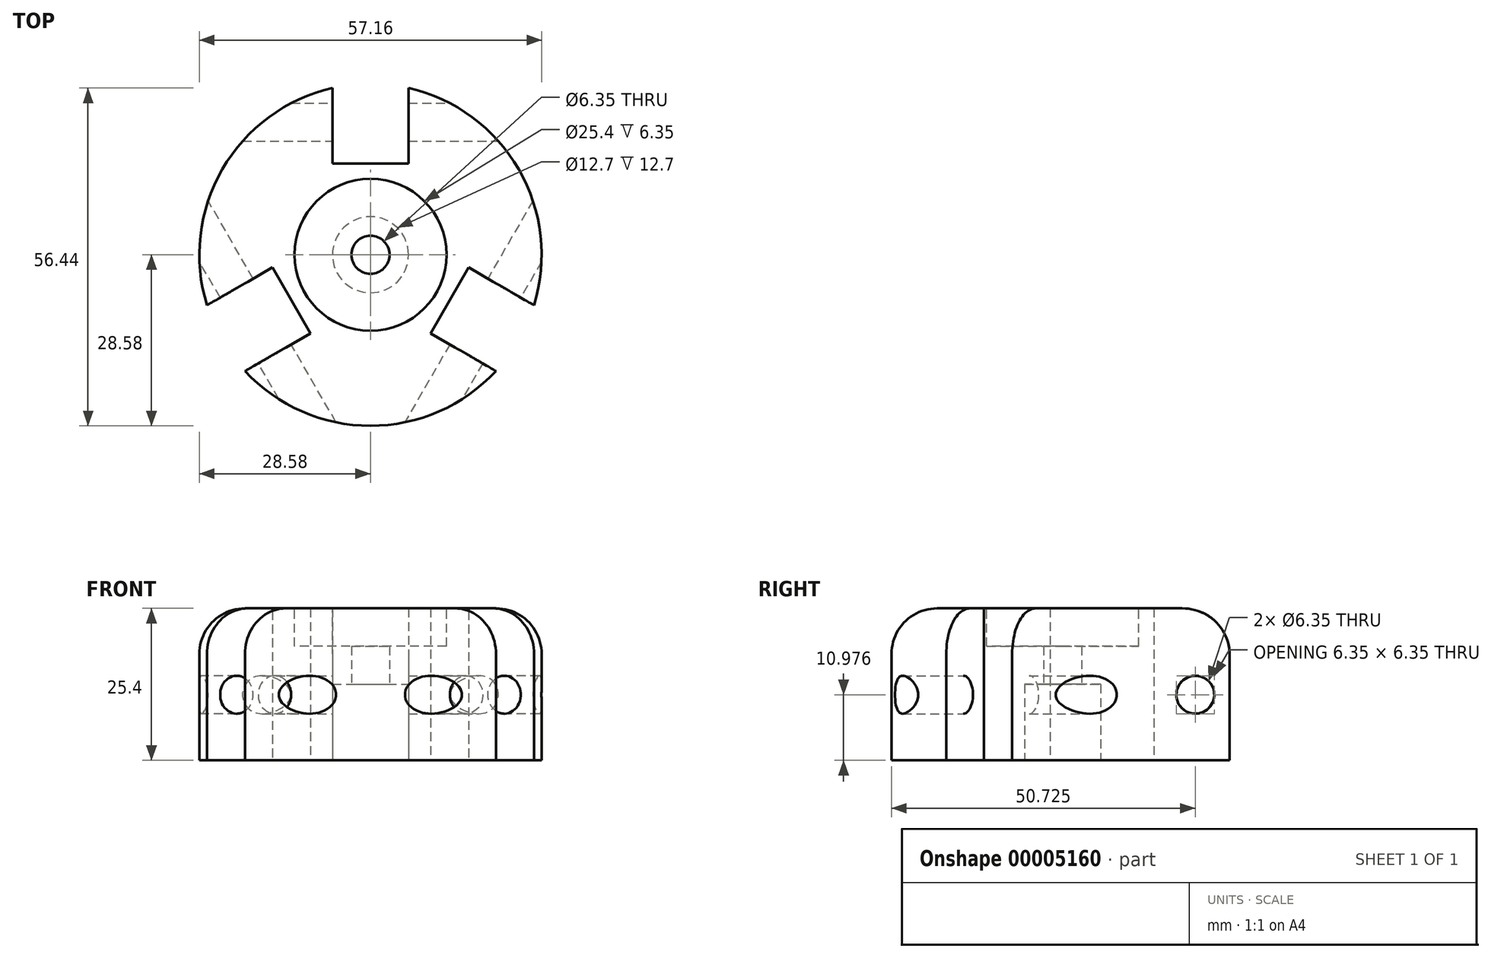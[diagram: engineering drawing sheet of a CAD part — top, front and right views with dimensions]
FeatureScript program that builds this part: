
annotation { "Feature Type Name" : "Feature", "Feature Type Description" : "" }
export const myFeature = defineFeature(function(context is Context, id is Id, definition is map)
    precondition{}
    {
        {
            var Q0;
            Q0=qCreatedBy(makeId("Top.planeOp"),FACE);
            var sketch = newSketch(context, id + "F0", { "sketchPlane" : qUnion([Q0])});
            skCircle(sketch, "E0", {"center": v(0, 0) * mm, "radius": 28.58 * mm});
            skLineSegment(sketch, "E1", {"start": v(0, 0) * mm, "end": v(0, 69.75) * mm, "construction": true});
            skLineSegment(sketch, "E2", {"start": v(0, 0) * mm, "end": v(65.6, -37.87) * mm, "construction": true});
            skLineSegment(sketch, "E3", {"start": v(0, 0) * mm, "end": v(-65.42, -37.77) * mm, "construction": true});
            skLineSegment(sketch, "E4.bottom", {"start": v(6.35, 15.24) * mm, "end": v(-6.35, 15.24) * mm});
            skLineSegment(sketch, "E4.top", {"start": v(6.35, 65.17) * mm, "end": v(-6.35, 65.17) * mm});
            skLineSegment(sketch, "E4.left", {"start": v(6.35, 15.24) * mm, "end": v(6.35, 65.17) * mm});
            skLineSegment(sketch, "E4.right", {"start": v(-6.35, 15.24) * mm, "end": v(-6.35, 65.17) * mm});
            skSolve(sketch);
        }
        {
            var Q0;
            {var subQ3=sQuery(id+"F0.wireOp",EDGE,"E4.bottom");Q0=makeQuery(id+"F0.imprint","IMPRINT",FACE,{"disambiguationData":[TD([[makeQuery(id+"F0.imprint","IMPRINT",EDGE,{"derivedFrom":subQ3}),1.0]])]});}
            extrude(context, id + "F1", {"entities" : qUnion([Q0]), "depth" : 25.4 * mm});
        }
        {
            var Q0;
            Q0=makeQuery(id+"F1.opExtrude","SWEPT_FACE",FACE,{"disambiguationData":[OSD([sQuery(id+"F0.wireOp",EDGE,"E4.bottom")])]});
            var Q1;
            Q1=makeQuery(id+"F1.opExtrude","SWEPT_FACE",FACE,{"disambiguationData":[OSD([sQuery(id+"F0.wireOp",EDGE,"E4.left")])]});
            var Q2;
            Q2=makeQuery(id+"F1.opExtrude","SWEPT_FACE",FACE,{"disambiguationData":[OSD([sQuery(id+"F0.wireOp",EDGE,"E4.right")])]});
            var Q3;
            Q3=makeQuery(id+"F1.opExtrude","CAP_EDGE",EDGE,{"disambiguationData":[OSD([sQuery(id+"F0.wireOp",EDGE,"E0")])],"isStart":false});
            circularPattern(context, id + "F2", {"faces" : qUnion([Q0, Q1, Q2]), "axis" : qUnion([Q3]), "angle" : 120 * degree, "instanceCount" : 3, "oppositeDirection" : true, "patternType" : PatternType.FACE});
        }
        {
            var Q0;
            Q0=makeQuery(id+"F1.opExtrude","SWEPT_FACE",FACE,{"disambiguationData":[OSD([sQuery(id+"F0.wireOp",EDGE,"E4.right")])]});
            var sketch = newSketch(context, id + "F3", { "sketchPlane" : qUnion([Q0])});
            skCircle(sketch, "E5", {"center": v(22.15, 10.98) * mm, "radius": 3.18 * mm});
            skSolve(sketch);
        }
        {
            var Q0;
            Q0=makeQuery(id+"F3.imprint","IMPRINT",FACE,{"disambiguationData":[TD([[makeQuery(id+"F3.imprint","IMPRINT",EDGE,{"derivedFrom":sQuery(id+"F3.wireOp",EDGE,"E5")}),1.0]])]});
            var Q1;
            Q1=sQuery(id+"F3.wireOp",EDGE,"E5");
            extrude(context, id + "F4", {"entities" : qUnion([Q0]), "operationType" : NewBodyOperationType.REMOVE, "surfaceEntities" : qUnion([Q1]), "endBound" : BoundingType.SYMMETRIC, "oppositeDirection" : true, "depth" : 101.6 * mm});
        }
        {
            var Q0;
            Q0=makeQuery(id+"F4.boolean.opBoolean","COPY",FACE,{"disambiguationData":[OD(1.0)],"derivedFrom":makeQuery(id+"F4.opExtrude","SWEPT_FACE",FACE,{"disambiguationData":[OSD([sQuery(id+"F3.wireOp",EDGE,"E5")])]})});
            var Q1;
            Q1=makeQuery(id+"F4.boolean.opBoolean","COPY",FACE,{"disambiguationData":[OD(0.0)],"derivedFrom":makeQuery(id+"F4.opExtrude","SWEPT_FACE",FACE,{"disambiguationData":[OSD([sQuery(id+"F3.wireOp",EDGE,"E5")])]})});
            var Q2;
            Q2=makeQuery(id+"F2.opPattern","SPLIT",EDGE,{"disambiguationData":[OD(0.0)],"derivedFrom":makeQuery(id+"F1.opExtrude","CAP_EDGE",EDGE,{"disambiguationData":[OSD([sQuery(id+"F0.wireOp",EDGE,"E0")])],"isStart":false})});
            circularPattern(context, id + "F5", {"faces" : qUnion([Q0, Q1]), "axis" : qUnion([Q2]), "angle" : 120 * degree, "instanceCount" : 3, "oppositeDirection" : true, "patternType" : PatternType.FACE});
        }
        {
            var Q0;
            Q0=makeQuery(id+"F1.opExtrude","CAP_FACE",FACE,{"disambiguationData":[OSD([sQuery(id+"F0.wireOp",EDGE,"E0"),sQuery(id+"F0.wireOp",EDGE,"E4.bottom"),sQuery(id+"F0.wireOp",EDGE,"E4.left"),sQuery(id+"F0.wireOp",EDGE,"E4.right")])],"isStart":false});
            var sketch = newSketch(context, id + "F6", { "sketchPlane" : qUnion([Q0])});
            skCircle(sketch, "E6", {"center": v(0, 0) * mm, "radius": 12.7 * mm});
            skSolve(sketch);
        }
        {
            var Q0;
            Q0=makeQuery(id+"F6.imprint","IMPRINT",FACE,{"disambiguationData":[TD([[makeQuery(id+"F6.imprint","IMPRINT",EDGE,{"derivedFrom":sQuery(id+"F6.wireOp",EDGE,"E6")}),1.0]])]});
            extrude(context, id + "F7", {"entities" : qUnion([Q0]), "operationType" : NewBodyOperationType.REMOVE, "oppositeDirection" : true, "depth" : 6.35 * mm});
        }
        {
            var Q0;
            Q0=makeQuery(id+"F1.opExtrude","CAP_FACE",FACE,{"disambiguationData":[OSD([sQuery(id+"F0.wireOp",EDGE,"E0"),sQuery(id+"F0.wireOp",EDGE,"E4.bottom"),sQuery(id+"F0.wireOp",EDGE,"E4.left"),sQuery(id+"F0.wireOp",EDGE,"E4.right")])],"isStart":true});
            var sketch = newSketch(context, id + "F8", { "sketchPlane" : qUnion([Q0])});
            skCircle(sketch, "E7", {"center": v(0, 0) * mm, "radius": 3.18 * mm});
            skCircle(sketch, "E8", {"center": v(0, 0) * mm, "radius": 6.35 * mm});
            skSolve(sketch);
        }
        {
            var Q0;
            Q0=makeQuery(id+"F8.imprint","IMPRINT",FACE,{"disambiguationData":[TD([[makeQuery(id+"F8.imprint","IMPRINT",EDGE,{"derivedFrom":sQuery(id+"F8.wireOp",EDGE,"E7")}),1.0]])]});
            extrude(context, id + "F9", {"entities" : qUnion([Q0]), "operationType" : NewBodyOperationType.REMOVE, "endBound" : BoundingType.THROUGH_ALL, "oppositeDirection" : true, "depth" : 25.4 * mm});
        }
        {
            var Q0;
            Q0=makeQuery(id+"F8.imprint","IMPRINT",FACE,{"disambiguationData":[TD([[makeQuery(id+"F8.imprint","IMPRINT",EDGE,{"derivedFrom":sQuery(id+"F8.wireOp",EDGE,"E7")}),-1.0]])]});
            extrude(context, id + "F10", {"entities" : qUnion([Q0]), "operationType" : NewBodyOperationType.REMOVE, "oppositeDirection" : true, "depth" : 12.7 * mm});
        }
        {
            var Q0;
            Q0=makeQuery(id+"F2.opPattern","SPLIT",EDGE,{"disambiguationData":[OD(2.0)],"derivedFrom":makeQuery(id+"F1.opExtrude","CAP_EDGE",EDGE,{"disambiguationData":[OSD([sQuery(id+"F0.wireOp",EDGE,"E0")])],"isStart":false})});
            var Q1;
            Q1=makeQuery(id+"F2.opPattern","SPLIT",EDGE,{"disambiguationData":[OD(1.0)],"derivedFrom":makeQuery(id+"F1.opExtrude","CAP_EDGE",EDGE,{"disambiguationData":[OSD([sQuery(id+"F0.wireOp",EDGE,"E0")])],"isStart":false})});
            var Q2;
            Q2=makeQuery(id+"F2.opPattern","SPLIT",EDGE,{"disambiguationData":[OD(0.0)],"derivedFrom":makeQuery(id+"F1.opExtrude","CAP_EDGE",EDGE,{"disambiguationData":[OSD([sQuery(id+"F0.wireOp",EDGE,"E0")])],"isStart":false})});
            fillet(context, id + "F11", {"entities" : qUnion([Q0, Q1, Q2]), "radius" : 7.62 * mm, "tangentPropagation" : true, "allowEdgeOverflow" : false});
        }
    });
